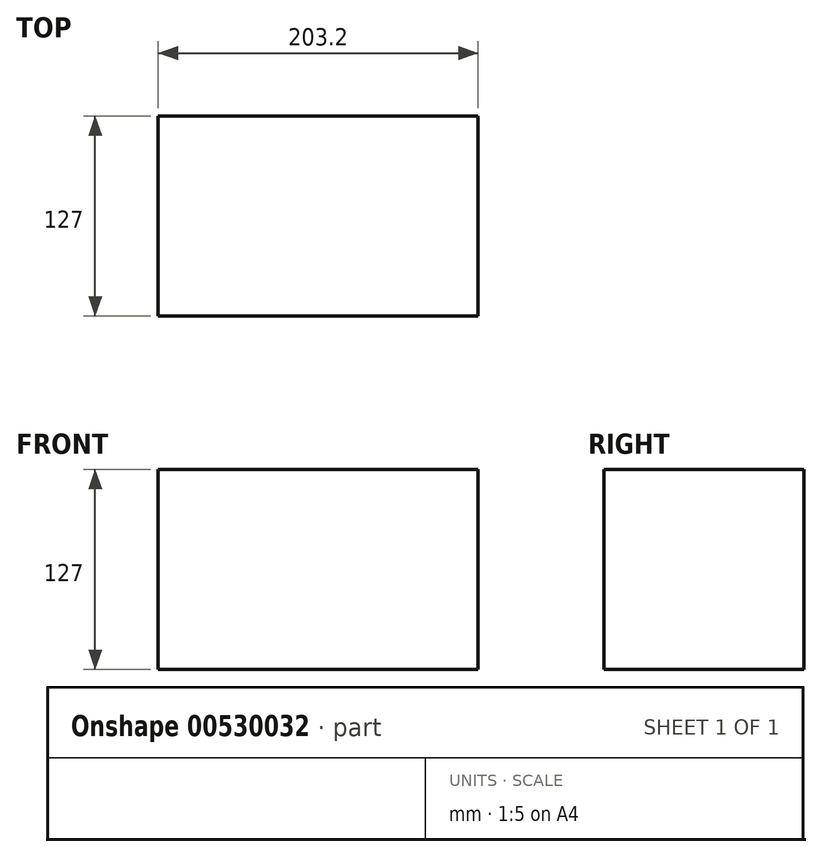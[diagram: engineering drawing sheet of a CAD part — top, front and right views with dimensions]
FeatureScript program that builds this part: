
annotation { "Feature Type Name" : "Feature", "Feature Type Description" : "" }
export const myFeature = defineFeature(function(context is Context, id is Id, definition is map)
    precondition{}
    {
        {
            var Q0;
            Q0=qCreatedBy(makeId("Top.planeOp"),FACE);
            var sketch = newSketch(context, id + "F0", { "sketchPlane" : qUnion([Q0])});
            skLineSegment(sketch, "E0.bottom", {"start": v(-101.6, 63.5) * mm, "end": v(101.6, 63.5) * mm});
            skLineSegment(sketch, "E0.top", {"start": v(-101.6, -63.5) * mm, "end": v(101.6, -63.5) * mm});
            skLineSegment(sketch, "E0.left", {"start": v(-101.6, 63.5) * mm, "end": v(-101.6, -63.5) * mm});
            skLineSegment(sketch, "E0.right", {"start": v(101.6, 63.5) * mm, "end": v(101.6, -63.5) * mm});
            skPoint(sketch, "E0.middle", {"position": v(0, 0) * mm});
            skLineSegment(sketch, "E1", {"start": v(-101.6, 0) * mm, "end": v(101.6, 0) * mm});
            skLineSegment(sketch, "E2", {"start": v(0, -63.5) * mm, "end": v(0, 63.5) * mm});
            skSolve(sketch);
        }
        {
            var Q0;
            {var subQ0=sQuery(id+"F0.wireOp",EDGE,"E0.left");var subQ1=sQuery(id+"F0.wireOp",EDGE,"E0.bottom");var subQ2=makeQuery(id+"F0.imprint","INTERSECT",VERTEX,{"derivedFrom":[subQ1,subQ0]});Q0=makeQuery(id+"F0.imprint","IMPRINT",FACE,{"disambiguationData":[TD([[makeQuery(id+"F0.imprint","IMPRINT",EDGE,{"disambiguationData":[TD([[subQ2,-1.0]])],"derivedFrom":subQ1}),-1.0]])]});}
            var Q1;
            {var subQ0=sQuery(id+"F0.wireOp",EDGE,"E0.left");var subQ1=sQuery(id+"F0.wireOp",EDGE,"E0.top");var subQ2=makeQuery(id+"F0.imprint","INTERSECT",VERTEX,{"derivedFrom":[subQ1,subQ0]});Q1=makeQuery(id+"F0.imprint","IMPRINT",FACE,{"disambiguationData":[TD([[makeQuery(id+"F0.imprint","IMPRINT",EDGE,{"disambiguationData":[TD([[subQ2,-1.0]])],"derivedFrom":subQ1}),1.0]])]});}
            extrude(context, id + "F1", {"entities" : qUnion([Q0, Q1]), "depth" : 127 * mm, "offsetDistance" : 25.4 * mm});
        }
        {
            var Q0;
            {var subQ0=sQuery(id+"F0.wireOp",EDGE,"E0.right");var subQ1=sQuery(id+"F0.wireOp",EDGE,"E0.bottom");var subQ2=makeQuery(id+"F0.imprint","INTERSECT",VERTEX,{"derivedFrom":[subQ1,subQ0]});Q0=makeQuery(id+"F0.imprint","IMPRINT",FACE,{"disambiguationData":[TD([[makeQuery(id+"F0.imprint","IMPRINT",EDGE,{"disambiguationData":[TD([[subQ2,1.0]])],"derivedFrom":subQ1}),-1.0]])]});}
            var Q1;
            {var subQ0=sQuery(id+"F0.wireOp",EDGE,"E0.right");var subQ1=sQuery(id+"F0.wireOp",EDGE,"E0.top");var subQ2=makeQuery(id+"F0.imprint","INTERSECT",VERTEX,{"derivedFrom":[subQ1,subQ0]});Q1=makeQuery(id+"F0.imprint","IMPRINT",FACE,{"disambiguationData":[TD([[makeQuery(id+"F0.imprint","IMPRINT",EDGE,{"disambiguationData":[TD([[subQ2,1.0]])],"derivedFrom":subQ1}),1.0]])]});}
            extrude(context, id + "F2", {"entities" : qUnion([Q0, Q1]), "operationType" : NewBodyOperationType.ADD, "depth" : 127 * mm, "offsetDistance" : 25.4 * mm});
        }
    });
